# Revit family: CWM
name_source: partatom
category: Lighting Fixtures
revit_build: Autodesk Revit 2014 (Build: 20130308_1515(x64)
units: mm (PartAtom-declared; Revit-internal decimal feet)

## types (2) — shared parameters
Certifications = All luminaires are built to UL 1598 and 2108 standards, and bear appropriate CSA labels. Damp location
labeling is standard. Emergency equipped fixtures labeled UL924. Adheres to LM79, LM80, and TM21
industry standards. NX is available in U.S., Canada and Mexico. For other locations consult factory.
Color Filter = 16777215
Description = CWM is a sleek, contemporary wall mount luminaire that provides unparalleled versatility and reliability, offering best-in-class efficacy with up to 109 Lumens per Watt.
Dimming Lamp Color Temperature Shift = <None>
Emit Shape Visible in Rendering = No
Emit from Rectangle Width = 2 "
Features = Simplistic modular design with interchangeable lenses and end caps
• The direct/indirect CWM is intended for ambient illumination such as corridors, overbed, and vanity
applications. Available in both semi‐recessed and flush mount configurations
• Direct/Indirect version comes available with multiple fascia styles including a straight, round, and
optional custom 3form inserts
• Four LED color choices and 84 CRI
• Long-life LEDs 60,000 hours at L80 with projected life over 86,000 hours for reduced life cycle
maintenance costs
• Easy removal of lens allows access to electrical components for modular replaceability
• Luminaire installs in three easy steps without disassembling the fixture
• Slender profile meets ADA requirements for wall mounted product
• Optional SpectraSync™ offers three modes of tunable white solutions and integrates seamlessly
into a variety of control systems
• NX Distributed Intelligence™ provides options for standalone and networked integrated sensor
with wired or wireless connectivity for NX system deployments
• CSA listed and suitable for damp locations
• 5 Year Warranty (Terms and Conditions apply
Glass = Glass - Hubbell - White
Housing = Paint - Hubbell - Matte White
Lamp = LED
Lighting Connector Description = Lighting Connector
Manufacturer = ColumbiaLighting
Model = Contemporary LED Wall Mount
Photometric Note = For More Photometric Web file please refer above link
Photometric Web Link = https://www.hubbell.com
Product Doucmentation Link = https://hubbellcdn.com
Product Name = CWM
Product Page URL = https://www.hubbell.com
Tilt Angle = 90.00°
Type Comments = Light Fixture
URL = https://www.hubbell.com
Warranty = Five year‐warranty standard. (Terms and Conditions Apply)

## per-type parameters (varying)
| type | Emit from Rectangle Length | Length | Photometric Web File |
| CWM-2' | 22 " | 24 " | CWM2-50MLxx-DISB-EDU.ies |
| CWM-4' | 46 " | 48 " | CWM4-35LWxx-DIC-EDU.ies |

## geometry (parser evidence)
native form markers: Sweep x2
no freeform markers — native parametric forms only
